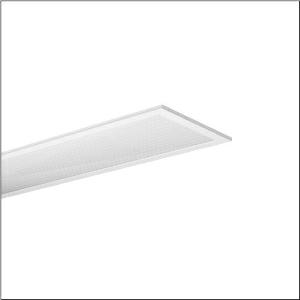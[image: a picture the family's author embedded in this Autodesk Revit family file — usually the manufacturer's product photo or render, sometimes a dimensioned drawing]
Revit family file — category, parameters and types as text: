
# Revit family: apollon_r__21_linear_51mq17wd2612_dc58
name_source: partatom
category: Lighting Fixtures
units: mm (PartAtom-declared; Revit-internal decimal feet)

## family parameters
Cut with Voids When Loaded = No
Host = Face
Light Source = No
Part Type = Normal
Room Calculation Point = No
Round Connector Dimension = Use Diameter
Shared = No

## types (1)
- Apollon® 21 linear (1 x LED, 6900 lm, 60 W, 6500K)
    Apparent Load = 60 VA
    CIE Flux Codes = 61 87 97 100 100
    Color Rendering = 80
    Color Temperature = 6500K
    Default Elevation = 1800 mm
    Description = Apollon® 21 linear, office luminaire, primary optical cover: micro prismatic cover, CAT 2 (L<= 3000cd/m²), light emission: direct distribution, primary light characteristic: symmetric, installation type: lay-in mounting, LED, rated luminous flux: 6.900lm, luminous efficacy: 115lm/W, light colour: 865, colour temperature: 6500K, with terminal, 5-pole, mains connection: 220..240V, AC, 50/60Hz, rated input power: 60W, housing, of aluminium, coated, pure white, length: 1.545mm, width: 307mm, height: 48mm, housing upper side, of sheet steel, galvanised, protection rating (complete): IP20, protection rating (lamp compartment, on room side): IP50, insulation class (complete): insulation class II (safety insulation), certification: CE, ENEC, packaging unit: 1 piece
    Height = 0 mm  [stored 0 ft]
    Lamp = 1 x LED
    Lamp Light Flux = 6900 lm
    Lamp Power = 60 W
    Lamp count = 1
    Length = 1545 mm
    Luminous efficacy = 115 lm/W
    Manufacturer = Siteco
    ModVariant = No
    Model = 51MQ17WD2612
    Mounting Place = Ceiling
    Mounting Type = Recessed
    Number of Poles = 1
    OnlyDefault = Yes
    Power Factor = 1
    Product Name = Apollon® 21 linear
    Product group = office luminaire | ceiling recessed
    ProductGroupID = 401
    Protection Class = Protection class II
    Protection Degree = IP 20
    RLX_Detail_Level = 1
    RLX_Emergency_Light_Flux = 0 lm
    RLX_Emergency_Type = 0
    RLX_Emergency_Type_DB = No
    RlxData = <blob elided: 17229 chars, md5=66775543>
    Socket = socket
    Standby Power = 0 W
    System Light Flux = 6900 lm
    System Power = 60 W
    Type Comments = Product without accessories
    Type Image = l_1291045.jpg
    URL = http://relux.com
    VarID = ---
    Voltage = 0 V
    Weight = 0.00 kg
    Width = 307 mm

note: [stored X ft] marks values corroborated as IEEE doubles in the binary element streams (Revit-internal decimal feet)

## geometry (parser evidence)
native form markers: Blend x4, Sweep x11
no freeform markers — native parametric forms only
